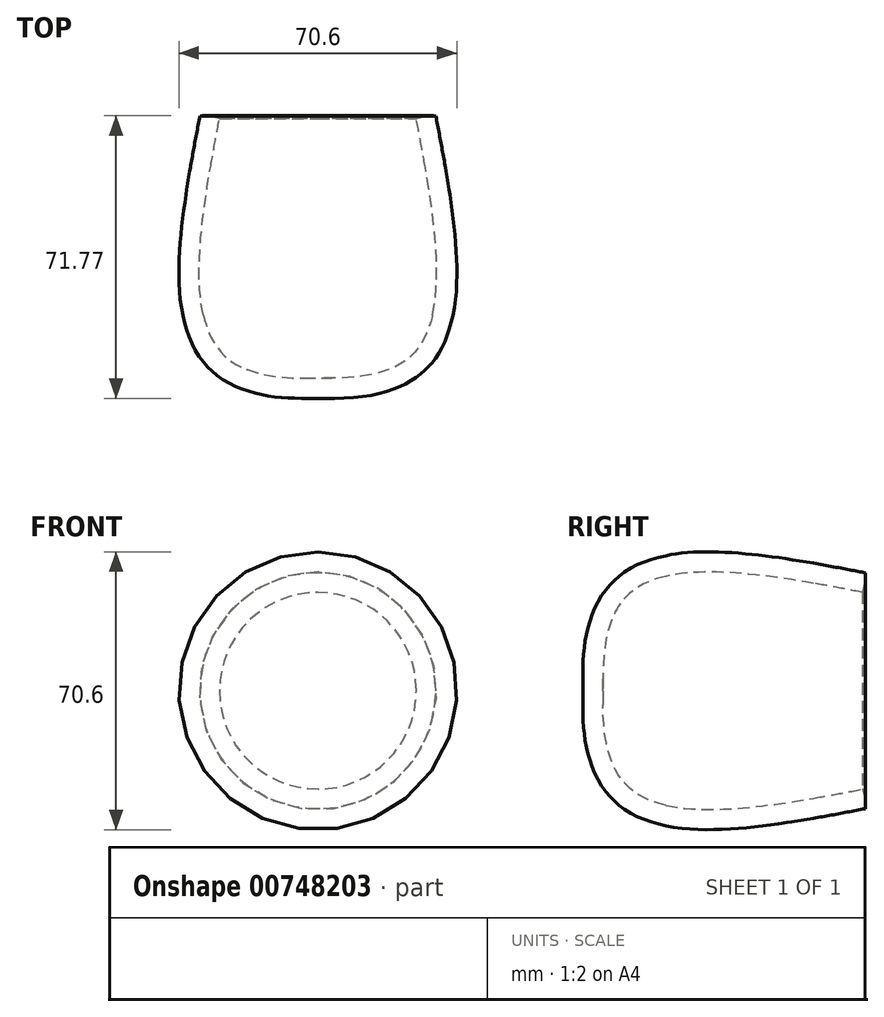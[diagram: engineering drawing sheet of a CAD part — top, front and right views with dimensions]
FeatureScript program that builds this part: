
annotation { "Feature Type Name" : "Feature", "Feature Type Description" : "" }
export const myFeature = defineFeature(function(context is Context, id is Id, definition is map)
    precondition{}
    {
        {
            var Q0;
            Q0=qCreatedBy(makeId("Top.planeOp"),FACE);
            var sketch = newSketch(context, id + "F0", { "sketchPlane" : qUnion([Q0])});
            skFitSpline(sketch, "E0", {"points": [v(24.45, 36.96) * mm, v(24.17, -25.72) * mm, v(-33.17, -27.12) * mm], "startDerivative": vector(29.28, -153.24) * mm, "endDerivative": vector(-145.82, 26.4) * mm});
            skLineSegment(sketch, "E1", {"start": v(0, 54.67) * mm, "end": v(0, -54.67) * mm});
            skFitSpline(sketch, "E2", {"points": [v(19.11, 30.78) * mm, v(27.55, 34.71) * mm, v(42.44, 31.62) * mm], "startDerivative": vector(17.6, 12.14) * mm, "endDerivative": vector(28.6, -9.57) * mm});
            skFitSpline(sketch, "E3.0", {"points": [v(29.36, 37.9) * mm, v(29.97, 34.7) * mm, v(31.2, 28.3) * mm, v(32.88, 18.8) * mm, v(34.24, 9.54) * mm, v(35.1, 0.7) * mm, v(35.27, -7.63) * mm, v(34.66, -14.05) * mm, v(33.56, -18.85) * mm, v(32.38, -22.25) * mm, v(30.77, -25.44) * mm, v(29.04, -27.86) * mm, v(27.4, -29.6) * mm, v(25.6, -31.19) * mm, v(23.15, -32.84) * mm, v(19.94, -34.36) * mm, v(15.39, -35.82) * mm, v(9.28, -36.79) * mm, v(1.37, -36.93) * mm, v(-7.05, -36.33) * mm, v(-15.86, -35.19) * mm, v(-24.92, -33.7) * mm, v(-31.02, -32.6) * mm, v(-34.06, -32.04) * mm]});
            skLineSegment(sketch, "E4", {"start": v(32.37, 21.6) * mm, "end": v(44.58, 21.6) * mm});
            skLineSegment(sketch, "E5", {"start": v(54.58, 11.6) * mm, "end": v(54.58, -5.9) * mm});
            skLineSegment(sketch, "E6", {"start": v(44.58, -15.9) * mm, "end": v(34.2, -15.9) * mm});
            skArc(sketch, "E7.filletArc", {"start": v(54.58, 11.6) * mm, "mid": v(51.65, 18.68) * mm, "end": v(44.58, 21.6) * mm});
            skArc(sketch, "E8.filletArc", {"start": v(44.58, -15.9) * mm, "mid": v(51.65, -12.97) * mm, "end": v(54.58, -5.9) * mm});
            skLineSegment(sketch, "E9", {"start": v(32.37, 21.6) * mm, "end": v(20.87, 21.6) * mm});
            skLineSegment(sketch, "E10", {"start": v(34.2, -15.9) * mm, "end": v(7.77, -15.9) * mm});
            skSolve(sketch);
        }
        {
            var Q0;
            {var subQ0=sQuery(id+"F0.wireOp",EDGE,"E1");var subQ1=sQuery(id+"F0.wireOp",EDGE,"E0");var subQ2=makeQuery(id+"F0.imprint","INTERSECT",VERTEX,{"derivedFrom":[subQ1,subQ0]});Q0=makeQuery(id+"F0.imprint","IMPRINT",FACE,{"disambiguationData":[TD([[makeQuery(id+"F0.imprint","IMPRINT",EDGE,{"disambiguationData":[TD([[subQ2,1.0]])],"derivedFrom":subQ1}),1.0]])]});}
            var Q1;
            {var subQ0=sQuery(id+"F0.wireOp",EDGE,"E9");var subQ1=sQuery(id+"F0.wireOp",EDGE,"E0");var subQ2=makeQuery(id+"F0.imprint","INTERSECT",VERTEX,{"derivedFrom":[subQ1,subQ0]});Q1=makeQuery(id+"F0.imprint","IMPRINT",FACE,{"disambiguationData":[TD([[makeQuery(id+"F0.imprint","IMPRINT",EDGE,{"disambiguationData":[TD([[subQ2,-1.0]])],"derivedFrom":subQ1}),1.0]])]});}
            var Q2;
            {var subQ0=sQuery(id+"F0.wireOp",EDGE,"E2");Q2=makeQuery(id+"F0.imprint","IMPRINT",FACE,{"disambiguationData":[TD([[makeQuery(id+"F0.imprint","IMPRINT",EDGE,{"derivedFrom":subQ0}),-1.0]])]});}
            var Q3;
            Q3=sQuery(id+"F0.wireOp",EDGE,"E1");
            revolve(context, id + "F1", {"surfaceOperationType" : NewSurfaceOperationType.NEW, "entities" : qUnion([Q0, Q1, Q2]), "axis" : qUnion([Q3]), "revolveType" : RevolveType.FULL});
        }
        {
            var Q0;
            Q0=sQuery(id+"F0.wireOp",VERTEX,"E9.end");
            var Q1;
            Q1=sQuery(id+"F0.wireOp",EDGE,"E9");
            cPlane(context, id + "F2", {"entities" : qUnion([Q0, Q1]), "cplaneType" : CPlaneType.LINE_POINT, "offset" : 25 * mm, "width" : 150 * mm, "height" : 150 * mm});
        }
        {
            var Q0;
            Q0=qCreatedBy(id+"F2.planeOp",FACE);
            var sketch = newSketch(context, id + "F3", { "sketchPlane" : qUnion([Q0])});
            skCircle(sketch, "E11", {"center": v(-18.95, 0) * mm, "radius": 2.7 * mm});
            skSolve(sketch);
        }
        {
            var Q0;
            Q0=makeQuery(id+"F3.imprint","IMPRINT",FACE,{"disambiguationData":[TD([[makeQuery(id+"F3.imprint","IMPRINT",EDGE,{"derivedFrom":sQuery(id+"F3.wireOp",EDGE,"E11")}),1.0]])]});
            var Q1;
            Q1=sQuery(id+"F0.wireOp",EDGE,"E9");
            var Q2;
            Q2=sQuery(id+"F0.wireOp",EDGE,"E4");
            var Q3;
            Q3=sQuery(id+"F0.wireOp",EDGE,"E7.filletArc");
            var Q4;
            Q4=sQuery(id+"F0.wireOp",EDGE,"E5");
            var Q5;
            Q5=sQuery(id+"F0.wireOp",EDGE,"E8.filletArc");
            var Q6;
            Q6=sQuery(id+"F0.wireOp",EDGE,"E6");
            var Q7;
            Q7=sQuery(id+"F0.wireOp",EDGE,"E10");
            sweep(context, id + "F4", {"profiles" : qUnion([Q0]), "path" : qUnion([Q1, Q2, Q3, Q4, Q5, Q6, Q7])});
        }
        {
            var Q0;
            Q0=makeQuery(id+"F1.opRevolve","SWEPT_BODY",BODY,{"disambiguationData":[OSD([sQuery(id+"F0.wireOp",EDGE,"E0"),sQuery(id+"F0.wireOp",EDGE,"E1"),sQuery(id+"F0.wireOp",EDGE,"E2"),sQuery(id+"F0.wireOp",EDGE,"E3.0")])]});
            var Q1;
            Q1=makeQuery(id+"F4.opSweep","SWEPT_BODY",BODY,{"disambiguationData":[OSD([sQuery(id+"F0.wireOp",EDGE,"E10"),sQuery(id+"F3.wireOp",EDGE,"E11")])]});
            booleanBodies(context, id + "F5", {"operationType" : BooleanOperationType.SUBTRACTION, "tools" : qUnion([Q0]), "targets" : qUnion([Q1]), "keepTools" : true});
        }
        {
            var Q0;
            Q0=makeQuery(id+"F5.opBoolean","SPLIT",BODY,{"disambiguationData":[OD(0.0)],"derivedFrom":makeQuery(id+"F4.opSweep","SWEPT_BODY",BODY,{"disambiguationData":[OSD([sQuery(id+"F0.wireOp",EDGE,"E10"),sQuery(id+"F3.wireOp",EDGE,"E11")])]})});
            var Q1;
            Q1=makeQuery(id+"F5.opBoolean","SPLIT",BODY,{"disambiguationData":[OD(1.0)],"derivedFrom":makeQuery(id+"F4.opSweep","SWEPT_BODY",BODY,{"disambiguationData":[OSD([sQuery(id+"F0.wireOp",EDGE,"E10"),sQuery(id+"F3.wireOp",EDGE,"E11")])]})});
            deleteBodies(context, id + "F6", {"entities" : qUnion([Q0, Q1])});
        }
        {
            var Q0;
            Q0=qCreatedBy(makeId("Top.planeOp"),FACE);
            var sketch = newSketch(context, id + "F7", { "sketchPlane" : qUnion([Q0])});
            skText(sketch, "E12", { "text": "EJH\n", "fontName": "OpenSans-Bold.ttf"});
            const initialGuessF7  = {"E12": [-0.0224, -0.0092, 1, 0, 0.0212]};
            skSetInitialGuess(sketch, initialGuessF7);
            skSolve(sketch);
        }
        {
            var Q0;
            Q0 = qSketchRegion(id + "F7", true);
            extrude(context, id + "F8", {"entities" : qUnion([Q0]), "depth" : 37 * mm, "offsetDistance" : 25 * mm});
        }
        {
            var Q0;
            Q0=makeQuery(id+"F1.opRevolve","SWEPT_BODY",BODY,{"disambiguationData":[OSD([sQuery(id+"F0.wireOp",EDGE,"E0"),sQuery(id+"F0.wireOp",EDGE,"E1"),sQuery(id+"F0.wireOp",EDGE,"E2"),sQuery(id+"F0.wireOp",EDGE,"E3.0")])]});
            var Q1;
            Q1=makeQuery(id+"F8.opExtrude","SWEPT_BODY",BODY,{"disambiguationData":[OSD([sQuery(id+"F7.wireOp",EDGE,"E12.sketch_text.stroke-22"),sQuery(id+"F7.wireOp",EDGE,"E12.sketch_text.stroke-23"),sQuery(id+"F7.wireOp",EDGE,"E12.sketch_text.stroke-24"),sQuery(id+"F7.wireOp",EDGE,"E12.sketch_text.stroke-25"),sQuery(id+"F7.wireOp",EDGE,"E12.sketch_text.stroke-26"),sQuery(id+"F7.wireOp",EDGE,"E12.sketch_text.stroke-27"),sQuery(id+"F7.wireOp",EDGE,"E12.sketch_text.stroke-28"),sQuery(id+"F7.wireOp",EDGE,"E12.sketch_text.stroke-29"),sQuery(id+"F7.wireOp",EDGE,"E12.sketch_text.stroke-30"),sQuery(id+"F7.wireOp",EDGE,"E12.sketch_text.stroke-31"),sQuery(id+"F7.wireOp",EDGE,"E12.sketch_text.stroke-32"),sQuery(id+"F7.wireOp",EDGE,"E12.sketch_text.stroke-33")])]});
            var Q2;
            Q2=makeQuery(id+"F8.opExtrude","SWEPT_BODY",BODY,{"disambiguationData":[OSD([sQuery(id+"F7.wireOp",EDGE,"E12.sketch_text.stroke-12"),sQuery(id+"F7.wireOp",EDGE,"E12.sketch_text.stroke-13"),sQuery(id+"F7.wireOp",EDGE,"E12.sketch_text.stroke-14"),sQuery(id+"F7.wireOp",EDGE,"E12.sketch_text.stroke-15"),sQuery(id+"F7.wireOp",EDGE,"E12.sketch_text.stroke-16"),sQuery(id+"F7.wireOp",EDGE,"E12.sketch_text.stroke-17"),sQuery(id+"F7.wireOp",EDGE,"E12.sketch_text.stroke-18"),sQuery(id+"F7.wireOp",EDGE,"E12.sketch_text.stroke-19"),sQuery(id+"F7.wireOp",EDGE,"E12.sketch_text.stroke-20"),sQuery(id+"F7.wireOp",EDGE,"E12.sketch_text.stroke-21")])]});
            var Q3;
            Q3=makeQuery(id+"F8.opExtrude","SWEPT_BODY",BODY,{"disambiguationData":[OSD([sQuery(id+"F7.wireOp",EDGE,"E12.sketch_text.stroke-0"),sQuery(id+"F7.wireOp",EDGE,"E12.sketch_text.stroke-1"),sQuery(id+"F7.wireOp",EDGE,"E12.sketch_text.stroke-2"),sQuery(id+"F7.wireOp",EDGE,"E12.sketch_text.stroke-3"),sQuery(id+"F7.wireOp",EDGE,"E12.sketch_text.stroke-4"),sQuery(id+"F7.wireOp",EDGE,"E12.sketch_text.stroke-5"),sQuery(id+"F7.wireOp",EDGE,"E12.sketch_text.stroke-6"),sQuery(id+"F7.wireOp",EDGE,"E12.sketch_text.stroke-7"),sQuery(id+"F7.wireOp",EDGE,"E12.sketch_text.stroke-8"),sQuery(id+"F7.wireOp",EDGE,"E12.sketch_text.stroke-9"),sQuery(id+"F7.wireOp",EDGE,"E12.sketch_text.stroke-10"),sQuery(id+"F7.wireOp",EDGE,"E12.sketch_text.stroke-11")])]});
            booleanBodies(context, id + "F9", {"operationType" : BooleanOperationType.SUBTRACTION, "tools" : qUnion([Q0]), "targets" : qUnion([Q1, Q2, Q3]), "keepTools" : true});
        }
        {
            var Q0;
            Q0=makeQuery(id+"F9.opBoolean","SPLIT",BODY,{"disambiguationData":[OD(0.0)],"derivedFrom":makeQuery(id+"F8.opExtrude","SWEPT_BODY",BODY,{"disambiguationData":[OSD([sQuery(id+"F7.wireOp",EDGE,"E12.sketch_text.stroke-22"),sQuery(id+"F7.wireOp",EDGE,"E12.sketch_text.stroke-23"),sQuery(id+"F7.wireOp",EDGE,"E12.sketch_text.stroke-24"),sQuery(id+"F7.wireOp",EDGE,"E12.sketch_text.stroke-25"),sQuery(id+"F7.wireOp",EDGE,"E12.sketch_text.stroke-26"),sQuery(id+"F7.wireOp",EDGE,"E12.sketch_text.stroke-27"),sQuery(id+"F7.wireOp",EDGE,"E12.sketch_text.stroke-28"),sQuery(id+"F7.wireOp",EDGE,"E12.sketch_text.stroke-29"),sQuery(id+"F7.wireOp",EDGE,"E12.sketch_text.stroke-30"),sQuery(id+"F7.wireOp",EDGE,"E12.sketch_text.stroke-31"),sQuery(id+"F7.wireOp",EDGE,"E12.sketch_text.stroke-32"),sQuery(id+"F7.wireOp",EDGE,"E12.sketch_text.stroke-33")])]})});
            var Q1;
            Q1=makeQuery(id+"F9.opBoolean","SPLIT",BODY,{"disambiguationData":[OD(0.0)],"derivedFrom":makeQuery(id+"F8.opExtrude","SWEPT_BODY",BODY,{"disambiguationData":[OSD([sQuery(id+"F7.wireOp",EDGE,"E12.sketch_text.stroke-12"),sQuery(id+"F7.wireOp",EDGE,"E12.sketch_text.stroke-13"),sQuery(id+"F7.wireOp",EDGE,"E12.sketch_text.stroke-14"),sQuery(id+"F7.wireOp",EDGE,"E12.sketch_text.stroke-15"),sQuery(id+"F7.wireOp",EDGE,"E12.sketch_text.stroke-16"),sQuery(id+"F7.wireOp",EDGE,"E12.sketch_text.stroke-17"),sQuery(id+"F7.wireOp",EDGE,"E12.sketch_text.stroke-18"),sQuery(id+"F7.wireOp",EDGE,"E12.sketch_text.stroke-19"),sQuery(id+"F7.wireOp",EDGE,"E12.sketch_text.stroke-20"),sQuery(id+"F7.wireOp",EDGE,"E12.sketch_text.stroke-21")])]})});
            var Q2;
            Q2=makeQuery(id+"F9.opBoolean","SPLIT",BODY,{"disambiguationData":[OD(0.0)],"derivedFrom":makeQuery(id+"F8.opExtrude","SWEPT_BODY",BODY,{"disambiguationData":[OSD([sQuery(id+"F7.wireOp",EDGE,"E12.sketch_text.stroke-0"),sQuery(id+"F7.wireOp",EDGE,"E12.sketch_text.stroke-1"),sQuery(id+"F7.wireOp",EDGE,"E12.sketch_text.stroke-2"),sQuery(id+"F7.wireOp",EDGE,"E12.sketch_text.stroke-3"),sQuery(id+"F7.wireOp",EDGE,"E12.sketch_text.stroke-4"),sQuery(id+"F7.wireOp",EDGE,"E12.sketch_text.stroke-5"),sQuery(id+"F7.wireOp",EDGE,"E12.sketch_text.stroke-6"),sQuery(id+"F7.wireOp",EDGE,"E12.sketch_text.stroke-7"),sQuery(id+"F7.wireOp",EDGE,"E12.sketch_text.stroke-8"),sQuery(id+"F7.wireOp",EDGE,"E12.sketch_text.stroke-9"),sQuery(id+"F7.wireOp",EDGE,"E12.sketch_text.stroke-10"),sQuery(id+"F7.wireOp",EDGE,"E12.sketch_text.stroke-11")])]})});
            deleteBodies(context, id + "F10", {"entities" : qUnion([Q0, Q1, Q2])});
        }
    });
